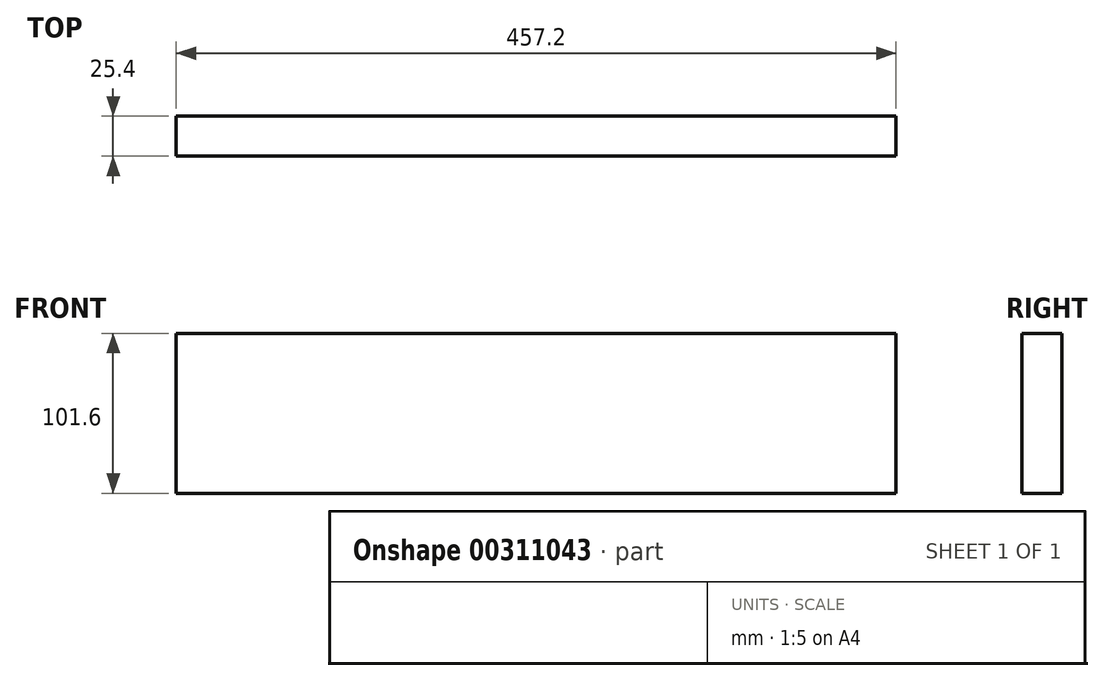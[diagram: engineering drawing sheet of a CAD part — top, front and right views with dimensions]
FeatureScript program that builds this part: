
annotation { "Feature Type Name" : "Feature", "Feature Type Description" : "" }
export const myFeature = defineFeature(function(context is Context, id is Id, definition is map)
    precondition{}
    {
        {
            var Q0;
            Q0=qCreatedBy(makeId("Front.planeOp"),FACE);
            var sketch = newSketch(context, id + "F0", { "sketchPlane" : qUnion([Q0])});
            skLineSegment(sketch, "E0.bottom", {"start": v(-328.76, 74.73) * mm, "end": v(128.44, 74.73) * mm});
            skLineSegment(sketch, "E0.top", {"start": v(-328.76, -26.87) * mm, "end": v(128.44, -26.87) * mm});
            skLineSegment(sketch, "E0.left", {"start": v(-328.76, 74.73) * mm, "end": v(-328.76, -26.87) * mm});
            skLineSegment(sketch, "E0.right", {"start": v(128.44, 74.73) * mm, "end": v(128.44, -26.87) * mm});
            skSolve(sketch);
        }
        {
            var Q0;
            Q0=makeQuery(id+"F0.imprint","IMPRINT",FACE,{"disambiguationData":[TD([[makeQuery(id+"F0.imprint","IMPRINT",EDGE,{"derivedFrom":sQuery(id+"F0.wireOp",EDGE,"E0.bottom")}),-1.0]])]});
            extrude(context, id + "F1", {"entities" : qUnion([Q0]), "depth" : 25.4 * mm});
        }
    });
